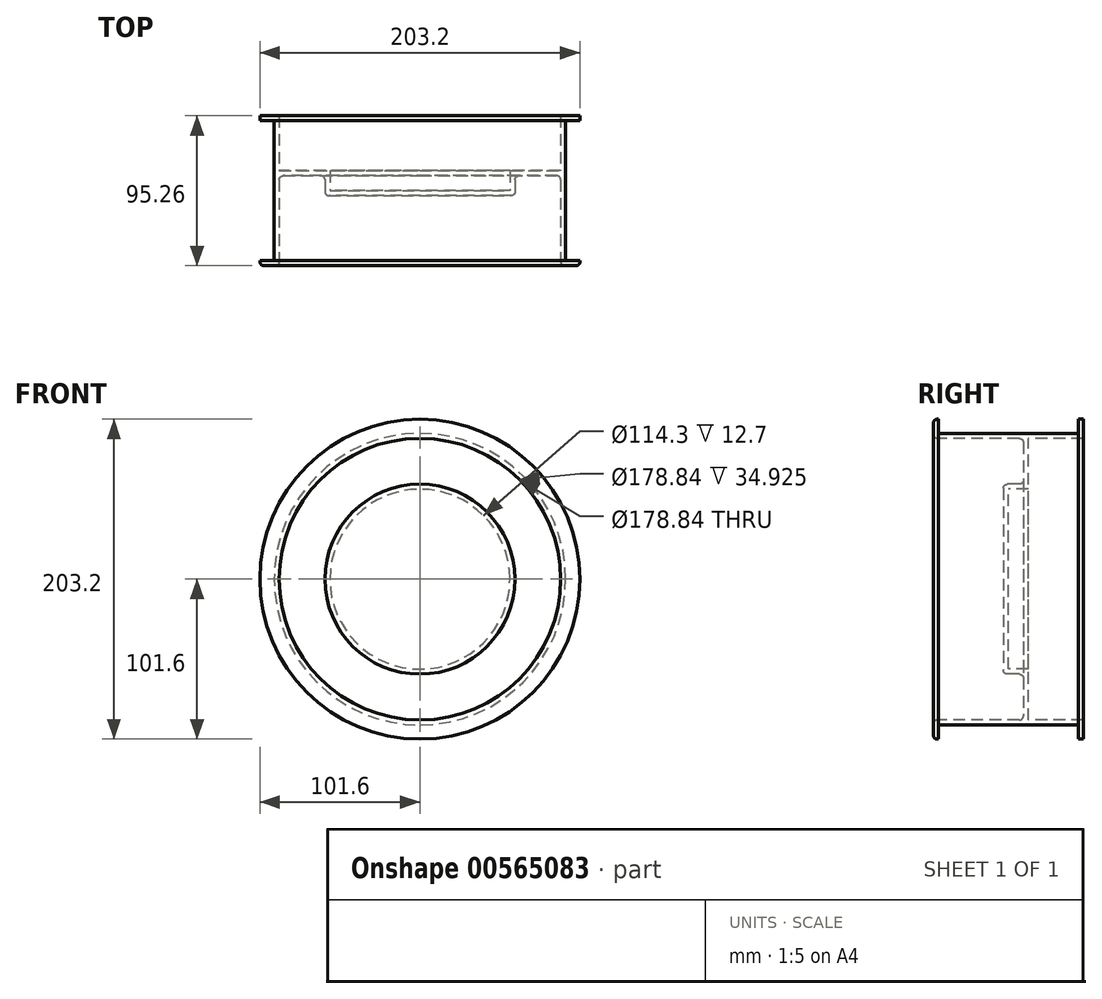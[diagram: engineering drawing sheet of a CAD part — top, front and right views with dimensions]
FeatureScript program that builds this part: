
annotation { "Feature Type Name" : "Feature", "Feature Type Description" : "" }
export const myFeature = defineFeature(function(context is Context, id is Id, definition is map)
    precondition{}
    {
        {
            var Q0;
            Q0=qCreatedBy(makeId("Right.planeOp"),FACE);
            var sketch = newSketch(context, id + "F0", { "sketchPlane" : qUnion([Q0])});
            skLineSegment(sketch, "E0", {"start": v(0, 0) * mm, "end": v(0, 57.15) * mm});
            skLineSegment(sketch, "E1", {"start": v(0, 57.15) * mm, "end": v(12.7, 57.15) * mm});
            skLineSegment(sketch, "E2", {"start": v(12.7, 57.15) * mm, "end": v(12.7, 89.42) * mm});
            skLineSegment(sketch, "E3", {"start": v(12.7, 89.42) * mm, "end": v(47.63, 89.42) * mm});
            skLineSegment(sketch, "E4", {"start": v(47.63, 89.42) * mm, "end": v(47.63, 101.6) * mm});
            skLineSegment(sketch, "E5", {"start": v(47.63, 101.6) * mm, "end": v(44.45, 101.6) * mm});
            skLineSegment(sketch, "E6", {"start": v(44.45, 101.6) * mm, "end": v(44.45, 92.6) * mm});
            skLineSegment(sketch, "E7", {"start": v(9.52, 89.42) * mm, "end": v(9.53, 60.33) * mm});
            skLineSegment(sketch, "E8", {"start": v(9.53, 60.33) * mm, "end": v(-3.18, 60.33) * mm});
            skLineSegment(sketch, "E9", {"start": v(-3.18, 60.33) * mm, "end": v(-3.17, 0) * mm});
            skLineSegment(sketch, "E10", {"start": v(-3.17, 0) * mm, "end": v(0, 0) * mm});
            skLineSegment(sketch, "E11", {"start": v(-44.45, 92.6) * mm, "end": v(-44.45, 101.6) * mm});
            skLineSegment(sketch, "E12", {"start": v(-44.45, 101.6) * mm, "end": v(-47.63, 101.6) * mm});
            skLineSegment(sketch, "E13", {"start": v(-47.63, 101.6) * mm, "end": v(-47.63, 89.42) * mm});
            skLineSegment(sketch, "E14", {"start": v(44.45, 92.6) * mm, "end": v(-44.45, 92.6) * mm});
            skLineSegment(sketch, "E15", {"start": v(-47.63, 89.42) * mm, "end": v(9.52, 89.42) * mm});
            skSolve(sketch);
        }
        {
            var Q0;
            Q0 = qSketchRegion(id + "F0", true);
            var Q1;
            Q1=sQuery(id+"F0.wireOp",EDGE,"E10");
            revolve(context, id + "F1", {"entities" : qUnion([Q0]), "axis" : qUnion([Q1]), "revolveType" : RevolveType.FULL});
        }
        {
            var Q0;
            Q0=makeQuery(id+"F1.opRevolve","SWEPT_FACE",FACE,{"disambiguationData":[OSD([sQuery(id+"F0.wireOp",EDGE,"E13")])]});
            var Q1;
            Q1=makeQuery(id+"F1.opRevolve","SWEPT_FACE",FACE,{"disambiguationData":[OSD([sQuery(id+"F0.wireOp",EDGE,"E7")])]});
            var Q2;
            Q2=makeQuery(id+"F1.opRevolve","SWEPT_FACE",FACE,{"disambiguationData":[OSD([sQuery(id+"F0.wireOp",EDGE,"E9")])]});
            fillet(context, id + "F2", {"entities" : qUnion([Q0, Q1, Q2]), "radius" : 2.54 * mm, "tangentPropagation" : true, "allowEdgeOverflow" : false});
        }
    });
